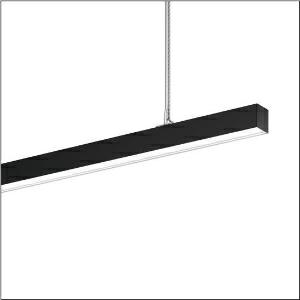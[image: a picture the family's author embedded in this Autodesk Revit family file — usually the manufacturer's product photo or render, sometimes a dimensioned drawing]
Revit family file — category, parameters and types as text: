
# Revit family: silica_r__21_51mx30dc49bb_d1ca
name_source: partatom
category: Lighting Fixtures
units: mm (PartAtom-declared; Revit-internal decimal feet)

## family parameters
Cut with Voids When Loaded = No
Host = Face
Light Source = No
Part Type = Normal
Room Calculation Point = No
Round Connector Dimension = Use Diameter
Shared = No

## types (1)
- --- (1 x LED, 10520 lm, 64.1 W, 4000K)
    Apparent Load = 64 VA
    CIE Flux Codes = 47 79 96 57 100
    Color Rendering = 80
    Color Temperature = 4000K
    Default Elevation = 1800 mm
    Description = Silica® 21, office luminaire, primary optical cover: cover, of PMMA, opal, light emission: direct/indirect distribution, primary light characteristic: symmetric, installation type: suspended mounting, LED, rated luminous flux: 10.520lm, luminous efficacy: 164lm/W, light colour: 840, colour temperature: 4000K, with terminal, 3+2-pole, max. 2.5mm², mains connection: 220..240V, AC, 50/60Hz, rated input power: 64.1W, luminaire housing, of aluminium, jet black (RAL 9005), length: 3.004mm, width: 53mm, height: 53mm, protection rating (complete): IP20, insulation class (complete): insulation class I (protective earthing), certification: CE, permissible operating ambient temperature: 0..+35°C, standard: EN 50419, packaging unit: 1 piece
    Height = 53 mm
    Lamp = 1 x LED
    Lamp Light Flux = 10520 lm
    Lamp Power = 64.1 W
    Lamp count = 1
    Length = 3004 mm
    Luminous efficacy = 164 lm/W
    Manufacturer = Siteco
    ModVariant = No
    Model = 51MX30DC49BB
    Mounting Place = Ceiling
    Mounting Type = Pendant
    Number of Poles = 1
    OnlyDefault = Yes
    Power Factor = 1
    Product Name = Silica® 21
    Product group = office luminaire | ceiling pendant
    ProductGroupID = 902
    Protection Class = Protection class I
    Protection Degree = IP 20
    RLX_Detail_Level = 1
    RLX_Emergency_Light_Flux = 0 lm
    RLX_Emergency_Type = 0
    RLX_Emergency_Type_DB = No
    RlxData = <blob elided: 25985 chars, md5=78706d67>
    Socket = socket
    Standby Power = 0 W
    System Light Flux = 10520 lm
    System Power = 64 W
    Type Comments = factory setting: luminous flux: 100 % | dim-lin: 254 | 218 mA
    Type Image = l_1297744.jpg
    URL = http://relux.com
    VarID = @adj_047307
    Voltage = 0 V
    Weight = 0.00 kg
    Width = 53 mm

## geometry (parser evidence)
native form markers: Blend x4, Sweep x13
no freeform markers — native parametric forms only
